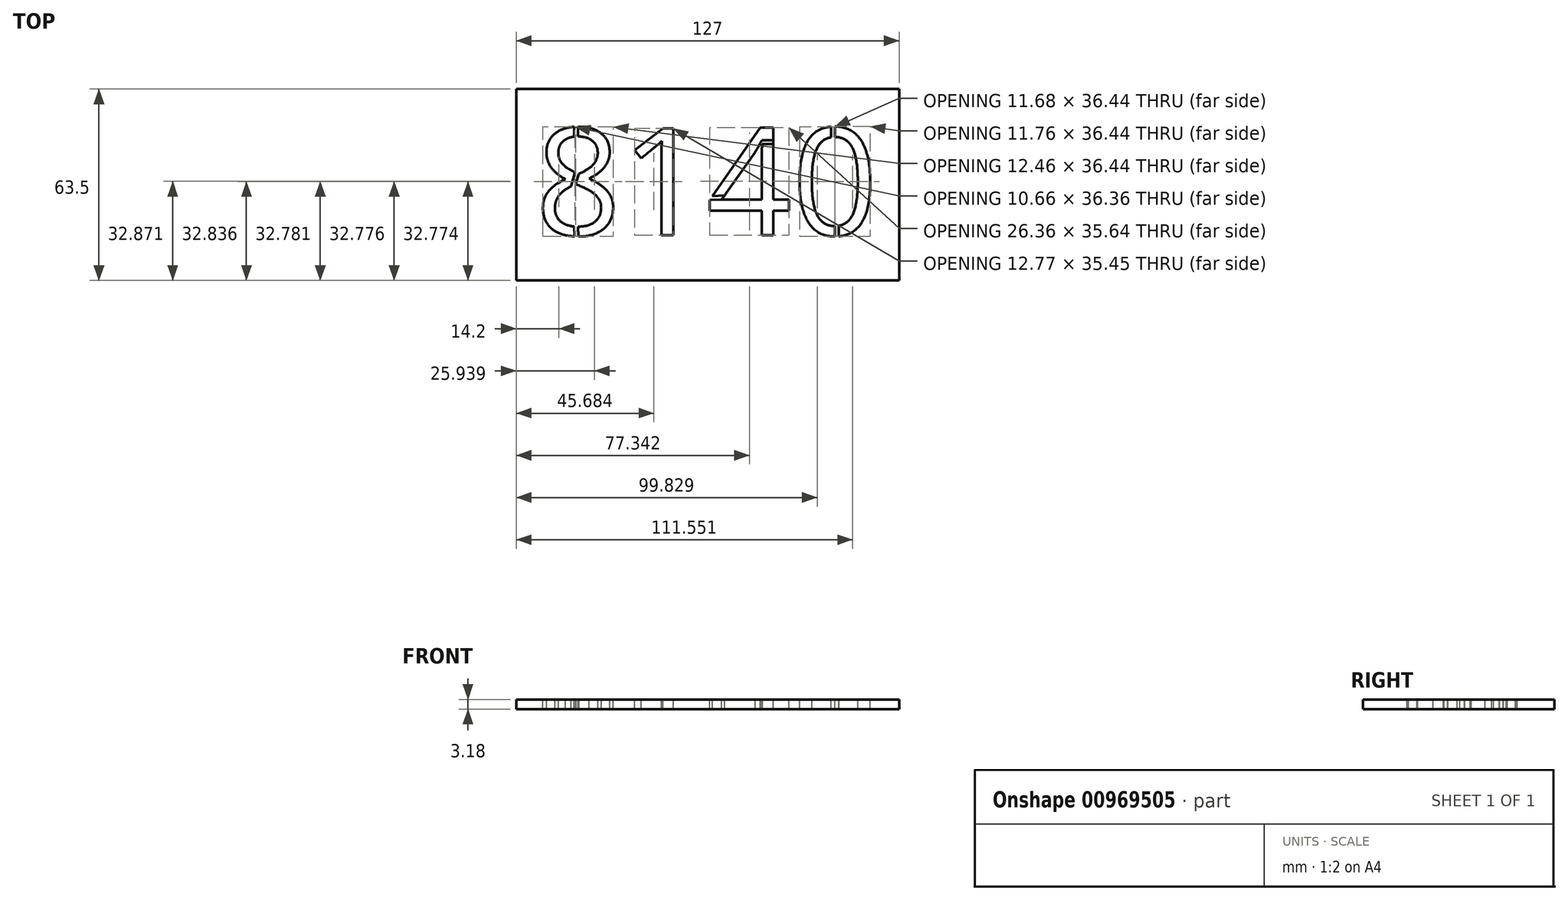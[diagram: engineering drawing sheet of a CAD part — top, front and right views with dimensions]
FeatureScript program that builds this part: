
annotation { "Feature Type Name" : "Feature", "Feature Type Description" : "" }
export const myFeature = defineFeature(function(context is Context, id is Id, definition is map)
    precondition{}
    {
        {
            var Q0;
            Q0=qCreatedBy(makeId("Top.planeOp"),FACE);
            var sketch = newSketch(context, id + "F0", { "sketchPlane" : qUnion([Q0])});
            skLineSegment(sketch, "E0.bottom", {"start": v(63.5, 31.75) * mm, "end": v(-63.5, 31.75) * mm});
            skLineSegment(sketch, "E0.top", {"start": v(63.5, -31.75) * mm, "end": v(-63.5, -31.75) * mm});
            skLineSegment(sketch, "E0.left", {"start": v(63.5, 31.75) * mm, "end": v(63.5, -31.75) * mm});
            skLineSegment(sketch, "E0.right", {"start": v(-63.5, 31.75) * mm, "end": v(-63.5, -31.75) * mm});
            skPoint(sketch, "E0.middle", {"position": v(0, 0) * mm});
            skSolve(sketch);
        }
        {
            var Q0;
            Q0=makeQuery(id+"F0.imprint","IMPRINT",FACE,{"disambiguationData":[TD([[makeQuery(id+"F0.imprint","IMPRINT",EDGE,{"derivedFrom":sQuery(id+"F0.wireOp",EDGE,"E0.bottom")}),1.0]])]});
            extrude(context, id + "F1", {"entities" : qUnion([Q0]), "depth" : 3.17 * mm, "offsetDistance" : 25.4 * mm});
        }
        {
            var Q0;
            Q0=makeQuery(id+"F1.opExtrude","CAP_FACE",FACE,{"disambiguationData":[OSD([sQuery(id+"F0.wireOp",EDGE,"E0.bottom"),sQuery(id+"F0.wireOp",EDGE,"E0.top"),sQuery(id+"F0.wireOp",EDGE,"E0.left"),sQuery(id+"F0.wireOp",EDGE,"E0.right")])],"isStart":false});
            var sketch = newSketch(context, id + "F2", { "sketchPlane" : qUnion([Q0])});
            skText(sketch, "E1", { "text": "8140", "fontName": "OpenSans-Regular.ttf"});
            const initialGuessF2  = {"E1": [-0.05715, -0.0167, 1, 0, 0.03575]};
            skSetInitialGuess(sketch, initialGuessF2);
            skSolve(sketch);
        }
        {
            var Q0;
            Q0 = qSketchRegion(id + "F2", true);
            extrude(context, id + "F3", {"entities" : qUnion([Q0]), "operationType" : NewBodyOperationType.REMOVE, "endBound" : BoundingType.UP_TO_NEXT, "oppositeDirection" : true, "depth" : 25.4 * mm, "offsetDistance" : 25.4 * mm});
        }
        {
            var Q0;
            {var subQ0=sQuery(id+"F0.wireOp",EDGE,"E0.left");var subQ1=sQuery(id+"F0.wireOp",EDGE,"E0.bottom");var subQ2=sQuery(id+"F0.wireOp",EDGE,"E0.right");var subQ3=sQuery(id+"F0.wireOp",EDGE,"E0.top");Q0=makeQuery(id+"F3.boolean.opBoolean","SPLIT",FACE,{"disambiguationData":[TD([makeQuery(id+"F1.opExtrude","SWEPT_FACE",FACE,{"disambiguationData":[OSD([subQ1])]})])],"derivedFrom":makeQuery(id+"F1.opExtrude","CAP_FACE",FACE,{"disambiguationData":[OSD([subQ1,subQ3,subQ0,subQ2])],"isStart":false})});}
            var sketch = newSketch(context, id + "F4", { "sketchPlane" : qUnion([Q0])});
            skLineSegment(sketch, "E2", {"start": v(-43, 19.25) * mm, "end": v(-43.04, 15.99) * mm});
            skLineSegment(sketch, "E3", {"start": v(-42.84, -17.19) * mm, "end": v(-42.94, -13.91) * mm});
            skLineSegment(sketch, "E4", {"start": v(0.66, -5.04) * mm, "end": v(4.69, -4.9) * mm});
            skLineSegment(sketch, "E5", {"start": v(-42.8, 3.62) * mm, "end": v(-43.8, 0.17) * mm});
            skLineSegment(sketch, "E6", {"start": v(21.76, 14.72) * mm, "end": v(18.15, 14.72) * mm});
            skLineSegment(sketch, "E7", {"start": v(42.17, 19.3) * mm, "end": v(42.17, 15.81) * mm});
            skLineSegment(sketch, "E8", {"start": v(42.17, -17.19) * mm, "end": v(42.17, -13.72) * mm});
            skLineSegment(sketch, "E9.0", {"start": v(-44.26, 19.2) * mm, "end": v(-44.3, 15.92) * mm});
            skLineSegment(sketch, "E10.0", {"start": v(-43.97, 4.13) * mm, "end": v(-45.32, -0.54) * mm});
            skLineSegment(sketch, "E11.0", {"start": v(-44.12, -17.16) * mm, "end": v(-44.22, -13.86) * mm});
            skLineSegment(sketch, "E12.0", {"start": v(21.76, 13.45) * mm, "end": v(18.08, 13.45) * mm});
            skLineSegment(sketch, "E13.0", {"start": v(1.58, -3.73) * mm, "end": v(5.6, -3.59) * mm});
            skLineSegment(sketch, "E14.0", {"start": v(40.9, 19.25) * mm, "end": v(40.9, 15.72) * mm});
            skLineSegment(sketch, "E15.0", {"start": v(43.44, -17.13) * mm, "end": v(43.44, -13.62) * mm});
            skArc(sketch, "E16", {"start": v(-43, 19.25) * mm, "mid": v(-43.63, 19.28) * mm, "end": v(-44.26, 19.2) * mm});
            skArc(sketch, "E17", {"start": v(-44.3, 15.92) * mm, "mid": v(-43.67, 15.93) * mm, "end": v(-43.04, 15.99) * mm});
            skArc(sketch, "E18", {"start": v(-42.8, 3.62) * mm, "mid": v(-43.35, 3.94) * mm, "end": v(-43.97, 4.13) * mm});
            skArc(sketch, "E19", {"start": v(-45.32, -0.54) * mm, "mid": v(-44.54, -0.22) * mm, "end": v(-43.8, 0.17) * mm});
            skArc(sketch, "E20", {"start": v(-42.94, -13.91) * mm, "mid": v(-43.58, -13.82) * mm, "end": v(-44.22, -13.86) * mm});
            skArc(sketch, "E21", {"start": v(-44.12, -17.16) * mm, "mid": v(-43.48, -17.2) * mm, "end": v(-42.84, -17.19) * mm});
            skLineSegment(sketch, "E22", {"start": v(5.6, -3.59) * mm, "end": v(4.69, -4.9) * mm});
            skLineSegment(sketch, "E23", {"start": v(1.58, -3.73) * mm, "end": v(0.66, -5.04) * mm});
            skLineSegment(sketch, "E24", {"start": v(18.15, 14.72) * mm, "end": v(18.08, 13.45) * mm});
            skLineSegment(sketch, "E25", {"start": v(21.76, 14.72) * mm, "end": v(21.76, 13.45) * mm});
            skArc(sketch, "E26", {"start": v(42.17, 19.3) * mm, "mid": v(41.53, 19.36) * mm, "end": v(40.9, 19.25) * mm});
            skArc(sketch, "E27", {"start": v(42.17, 15.81) * mm, "mid": v(41.53, 15.78) * mm, "end": v(40.9, 15.72) * mm});
            skArc(sketch, "E28", {"start": v(43.44, -13.62) * mm, "mid": v(42.8, -13.59) * mm, "end": v(42.17, -13.72) * mm});
            skArc(sketch, "E29", {"start": v(42.17, -17.19) * mm, "mid": v(42.8, -17.21) * mm, "end": v(43.44, -17.13) * mm});
            skSolve(sketch);
        }
        {
            var Q0;
            {var subQ0=sQuery(id+"F0.wireOp",EDGE,"E0.left");var subQ1=sQuery(id+"F0.wireOp",EDGE,"E0.bottom");var subQ2=sQuery(id+"F0.wireOp",EDGE,"E0.right");var subQ3=sQuery(id+"F0.wireOp",EDGE,"E0.top");Q0=makeQuery(id+"F3.boolean.opBoolean","SPLIT",FACE,{"disambiguationData":[TD([makeQuery(id+"F1.opExtrude","SWEPT_FACE",FACE,{"disambiguationData":[OSD([subQ1])]})])],"derivedFrom":makeQuery(id+"F1.opExtrude","CAP_FACE",FACE,{"disambiguationData":[OSD([subQ1,subQ3,subQ0,subQ2])],"isStart":true})});}
            var sketch = newSketch(context, id + "F5", { "sketchPlane" : qUnion([Q0])});
            skLineSegment(sketch, "E30", {"start": v(-43, -19.25) * mm, "end": v(-43.04, -15.99) * mm});
            skLineSegment(sketch, "E31", {"start": v(-42.8, -3.62) * mm, "end": v(-43.8, -0.17) * mm});
            skLineSegment(sketch, "E32", {"start": v(-42.94, 13.91) * mm, "end": v(-42.84, 17.19) * mm});
            skLineSegment(sketch, "E33", {"start": v(21.76, -14.72) * mm, "end": v(18.15, -14.72) * mm});
            skLineSegment(sketch, "E34", {"start": v(4.69, 4.9) * mm, "end": v(0.66, 5.04) * mm});
            skLineSegment(sketch, "E35", {"start": v(42.17, -15.81) * mm, "end": v(42.17, -19.3) * mm});
            skLineSegment(sketch, "E36", {"start": v(42.17, 13.72) * mm, "end": v(42.17, 17.19) * mm});
            skSolve(sketch);
        }
        {
            var Q0;
            Q0 = qSketchRegion(id + "F4", true);
            var Q1;
            {var subQ0=sQuery(id+"F0.wireOp",EDGE,"E0.left");var subQ1=sQuery(id+"F0.wireOp",EDGE,"E0.bottom");var subQ2=sQuery(id+"F0.wireOp",EDGE,"E0.right");var subQ3=sQuery(id+"F0.wireOp",EDGE,"E0.top");Q1=makeQuery(id+"F3.boolean.opBoolean","SPLIT",FACE,{"disambiguationData":[TD([makeQuery(id+"F1.opExtrude","SWEPT_FACE",FACE,{"disambiguationData":[OSD([subQ1])]})])],"derivedFrom":makeQuery(id+"F1.opExtrude","CAP_FACE",FACE,{"disambiguationData":[OSD([subQ1,subQ3,subQ0,subQ2])],"isStart":true})});}
            extrude(context, id + "F6", {"entities" : qUnion([Q0]), "operationType" : NewBodyOperationType.ADD, "endBound" : BoundingType.UP_TO_SURFACE, "oppositeDirection" : true, "depth" : 25.4 * mm, "endBoundEntityFace" : qUnion([Q1]), "offsetDistance" : 25.4 * mm});
        }
    });
